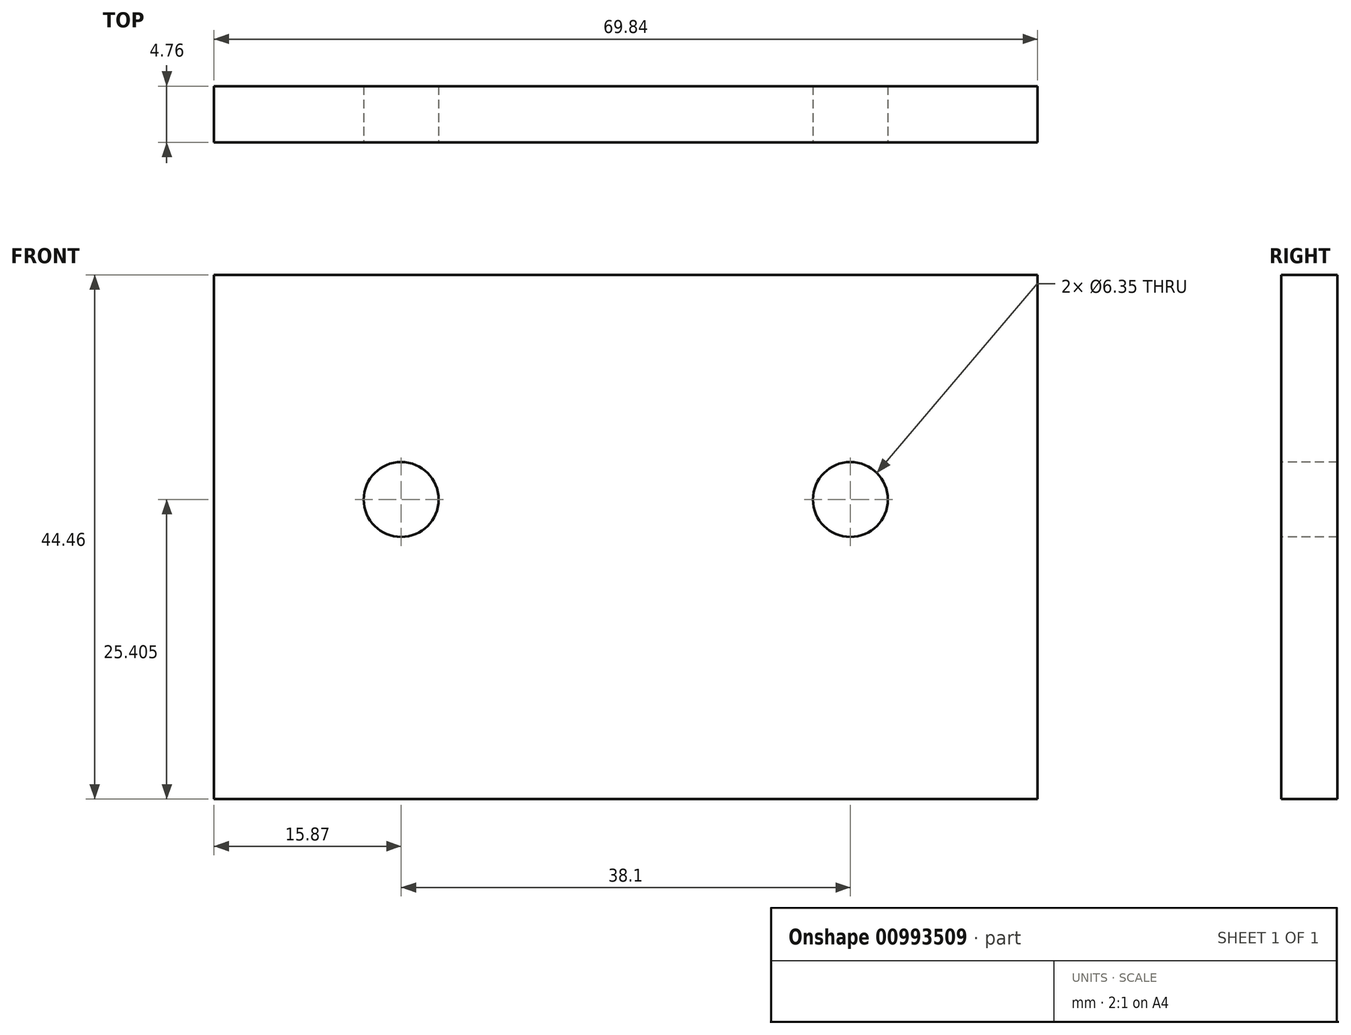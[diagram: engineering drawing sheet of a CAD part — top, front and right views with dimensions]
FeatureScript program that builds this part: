
annotation { "Feature Type Name" : "Feature", "Feature Type Description" : "" }
export const myFeature = defineFeature(function(context is Context, id is Id, definition is map)
    precondition{}
    {
        {
            var Q0;
            Q0=qCreatedBy(makeId("Front.planeOp"),FACE);
            var sketch = newSketch(context, id + "F0", { "sketchPlane" : qUnion([Q0])});
            skLineSegment(sketch, "E0.bottom", {"start": v(34.93, -22.22) * mm, "end": v(-34.93, -22.23) * mm});
            skLineSegment(sketch, "E0.top", {"start": v(34.93, 22.23) * mm, "end": v(-34.93, 22.22) * mm});
            skLineSegment(sketch, "E0.left", {"start": v(34.93, -22.22) * mm, "end": v(34.93, 22.23) * mm});
            skLineSegment(sketch, "E0.right", {"start": v(-34.93, -22.23) * mm, "end": v(-34.93, 22.22) * mm});
            skPoint(sketch, "E0.middle", {"position": v(0, 0) * mm});
            skSolve(sketch);
        }
        {
            var Q0;
            Q0=makeQuery(id+"F0.imprint","IMPRINT",FACE,{"disambiguationData":[TD([[makeQuery(id+"F0.imprint","IMPRINT",EDGE,{"derivedFrom":sQuery(id+"F0.wireOp",EDGE,"E0.bottom")}),-1.0]])]});
            extrude(context, id + "F1", {"entities" : qUnion([Q0]), "depth" : 4.76 * mm, "offsetDistance" : 25.4 * mm});
        }
        {
            var Q0;
            Q0=makeQuery(id+"F1.opExtrude","CAP_FACE",FACE,{"disambiguationData":[OSD([sQuery(id+"F0.wireOp",EDGE,"E0.bottom"),sQuery(id+"F0.wireOp",EDGE,"E0.top"),sQuery(id+"F0.wireOp",EDGE,"E0.left"),sQuery(id+"F0.wireOp",EDGE,"E0.right")])],"isStart":false});
            var sketch = newSketch(context, id + "F2", { "sketchPlane" : qUnion([Q0])});
            skLineSegment(sketch, "E1", {"start": v(34.93, -22.22) * mm, "end": v(34.93, 3.18) * mm});
            skLineSegment(sketch, "E2", {"start": v(34.93, 3.18) * mm, "end": v(19.05, 3.18) * mm});
            skCircle(sketch, "E3", {"center": v(19.05, 3.18) * mm, "radius": 3.18 * mm});
            skLineSegment(sketch, "E4", {"start": v(-34.93, -22.23) * mm, "end": v(-34.93, 3.17) * mm});
            skLineSegment(sketch, "E5", {"start": v(-34.93, 3.17) * mm, "end": v(-19.05, 3.17) * mm});
            skCircle(sketch, "E6", {"center": v(-19.05, 3.17) * mm, "radius": 3.18 * mm});
            skSolve(sketch);
        }
        {
            var Q0;
            Q0=makeQuery(id+"F2.imprint","IMPRINT",FACE,{"disambiguationData":[TD([[makeQuery(id+"F2.imprint","IMPRINT",EDGE,{"derivedFrom":sQuery(id+"F2.wireOp",EDGE,"E6")}),1.0]])]});
            var Q1;
            Q1=makeQuery(id+"F2.imprint","IMPRINT",FACE,{"disambiguationData":[TD([[makeQuery(id+"F2.imprint","IMPRINT",EDGE,{"derivedFrom":sQuery(id+"F2.wireOp",EDGE,"E3")}),1.0]])]});
            extrude(context, id + "F3", {"entities" : qUnion([Q0, Q1]), "operationType" : NewBodyOperationType.REMOVE, "oppositeDirection" : true, "depth" : 25.4 * mm, "offsetDistance" : 25.4 * mm});
        }
    });
